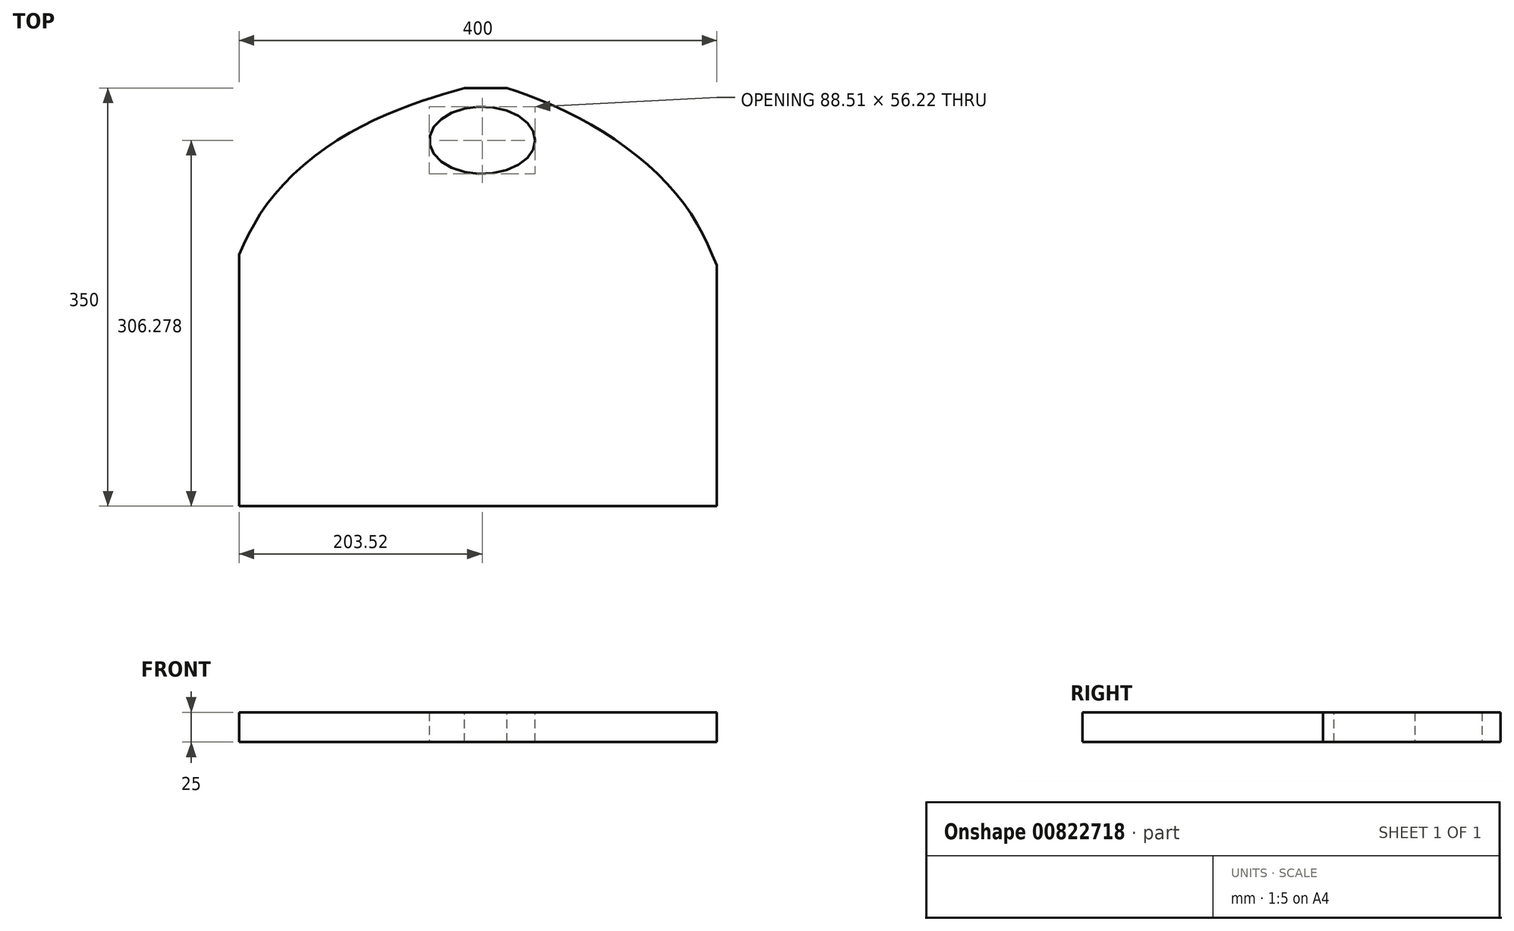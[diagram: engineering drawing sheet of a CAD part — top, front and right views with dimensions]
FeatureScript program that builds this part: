
annotation { "Feature Type Name" : "Feature", "Feature Type Description" : "" }
export const myFeature = defineFeature(function(context is Context, id is Id, definition is map)
    precondition{}
    {
        {
            var Q0;
            Q0=qCreatedBy(makeId("Top.planeOp"),FACE);
            var sketch = newSketch(context, id + "F0", { "sketchPlane" : qUnion([Q0])});
            skLineSegment(sketch, "E0.bottom", {"start": v(-203.52, 293.4) * mm, "end": v(196.48, 293.4) * mm});
            skLineSegment(sketch, "E0.top", {"start": v(-203.52, -56.6) * mm, "end": v(196.48, -56.6) * mm});
            skLineSegment(sketch, "E0.left", {"start": v(-203.52, 293.4) * mm, "end": v(-203.52, -56.6) * mm});
            skLineSegment(sketch, "E0.right", {"start": v(196.48, 293.4) * mm, "end": v(196.48, -56.6) * mm});
            skSolve(sketch);
        }
        {
            var Q0;
            Q0=makeQuery(id+"F0.imprint","IMPRINT",FACE,{"disambiguationData":[TD([[makeQuery(id+"F0.imprint","IMPRINT",EDGE,{"derivedFrom":sQuery(id+"F0.wireOp",EDGE,"E0.bottom")}),-1.0]])]});
            extrude(context, id + "F1", {"entities" : qUnion([Q0]), "depth" : 25 * mm, "offsetDistance" : 25 * mm});
        }
        {
            var Q0;
            Q0=makeQuery(id+"F1.opExtrude","CAP_FACE",FACE,{"disambiguationData":[OSD([sQuery(id+"F0.wireOp",EDGE,"E0.bottom"),sQuery(id+"F0.wireOp",EDGE,"E0.top"),sQuery(id+"F0.wireOp",EDGE,"E0.left"),sQuery(id+"F0.wireOp",EDGE,"E0.right")])],"isStart":false});
            var sketch = newSketch(context, id + "F2", { "sketchPlane" : qUnion([Q0])});
            skFitSpline(sketch, "E1", {"points": [v(-203.52, 154.12) * mm, v(-178.34, 198.75) * mm, v(-125.7, 246.82) * mm, v(-62.75, 278.29) * mm, v(-14.68, 293.4) * mm], "startDerivative": vector(91.52, 194.89) * mm, "endDerivative": vector(203.8, 57.4) * mm});
            skFitSpline(sketch, "E2", {"points": [v(20.8, 293.4) * mm, v(62, 277.72) * mm, v(123.22, 241.67) * mm, v(171.86, 192.46) * mm, v(196.48, 144.96) * mm], "startDerivative": vector(181.27, -61.43) * mm, "endDerivative": vector(87.68, -201.54) * mm});
            skEllipse(sketch, "E3", {"center": v(0, 249.68) * mm, "majorRadius": 44.26 * mm, "minorRadius": 28.11 * mm, "majorAxis": v(1, 0)});
            skSolve(sketch);
        }
        {
            var Q0;
            Q0 = qSketchRegion(id + "F2", true);
            var Q1;
            {var subQ0=sQuery(id+"F2.wireOp",EDGE,"E1");Q1=makeQuery(id+"F2.imprint","IMPRINT",FACE,{"disambiguationData":[TD([[makeQuery(id+"F2.imprint","IMPRINT",EDGE,{"derivedFrom":subQ0}),1.0]])]});}
            extrude(context, id + "F3", {"entities" : qUnion([Q0, Q1]), "operationType" : NewBodyOperationType.REMOVE, "endBound" : BoundingType.THROUGH_ALL, "oppositeDirection" : true, "depth" : 25 * mm, "offsetDistance" : 25 * mm});
        }
        {
            var Q0;
            {var subQ0=sQuery(id+"F2.wireOp",EDGE,"E2");Q0=makeQuery(id+"F2.imprint","IMPRINT",FACE,{"disambiguationData":[TD([[makeQuery(id+"F2.imprint","IMPRINT",EDGE,{"derivedFrom":subQ0}),1.0]])]});}
            extrude(context, id + "F4", {"entities" : qUnion([Q0]), "operationType" : NewBodyOperationType.REMOVE, "endBound" : BoundingType.THROUGH_ALL, "oppositeDirection" : true, "depth" : 25 * mm, "offsetDistance" : 25 * mm});
        }
    });
